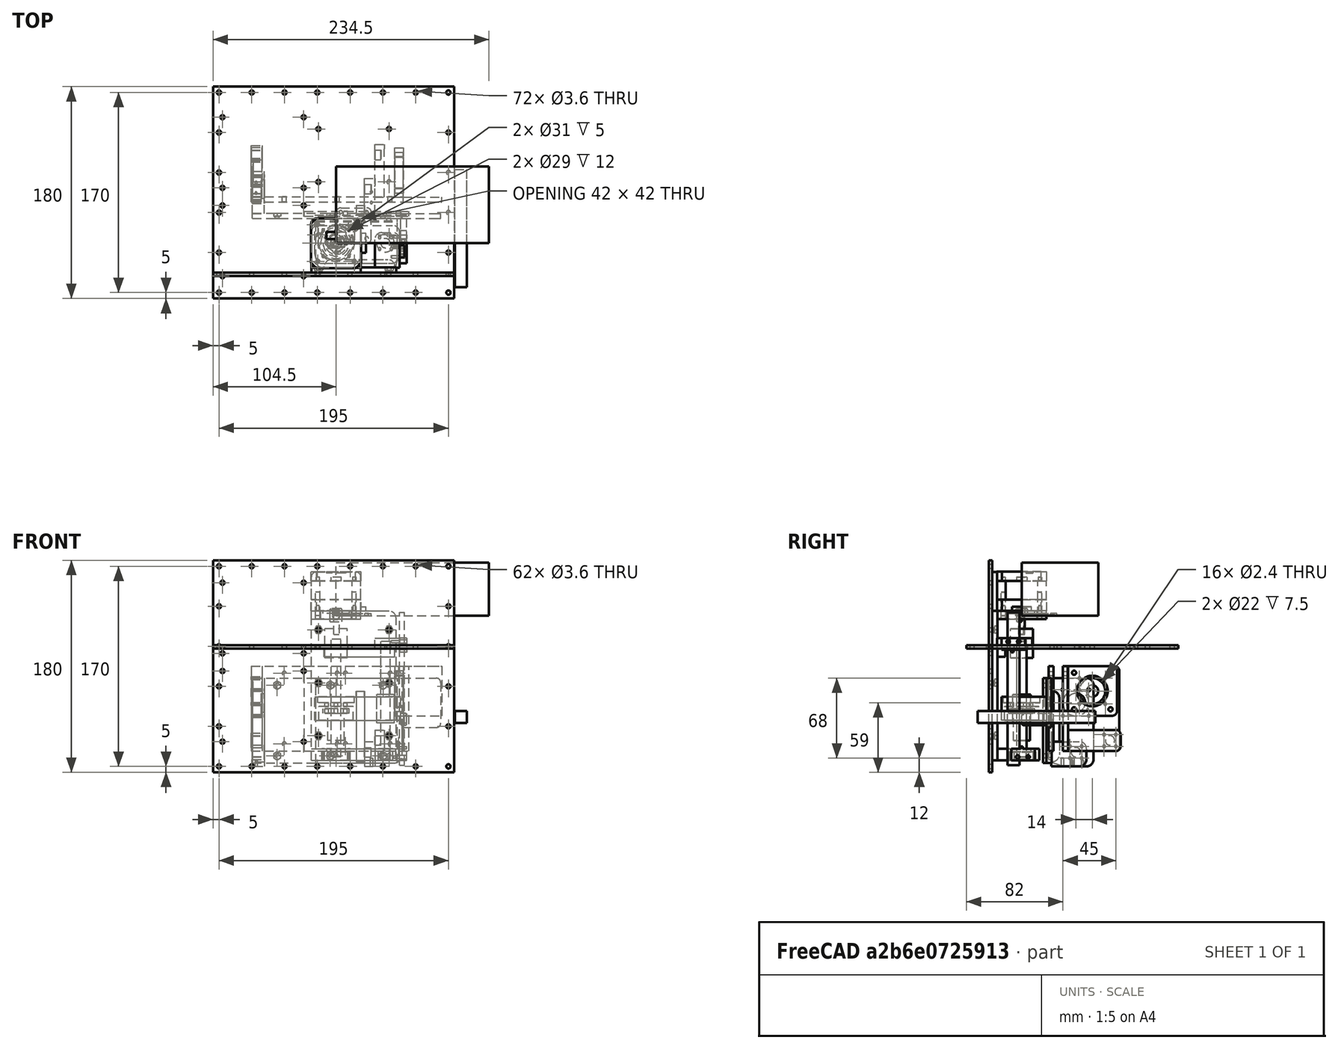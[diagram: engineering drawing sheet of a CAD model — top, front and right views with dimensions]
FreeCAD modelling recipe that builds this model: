
FCSTD DOCUMENT  (FreeCAD 0.18.4R)
Label: small_moving_desk
License: All rights reserved
LicenseURL: http://en.wikipedia.org/wiki/All_rights_reserved
objects: Part::Cylinder×33, Part::Box×21, Part::FeaturePython×18, Part::Cut×14, Part::MultiFuse×12, Part::Fillet×10, App::Part×9, PartDesign::FeatureBase×9, PartDesign::Body×9, Part::Feature×7, Part::Compound×5, Path::FeaturePython×4, Mesh::Feature×1, App::FeaturePython×1, App::DocumentObjectGroup×1, Path::FeatureCompoundPython×1, Part::RegularPolygon×1, Part::Extrusion×1
note: 141 computed .brp shape members not serialized (recipe doc carries the construction recipe); baked Part::Feature solids carry a one-line shape summary decoded from their .brp

FEATURE [Part::Feature] Pocket003Body001  label="StepperBody"
  Placement = pos=(0,0,4) rot=(0,0,1;0rad)
  shape: bbox 46.6 x 42.3 x 53.35 mm, 70 faces (baked)
FEATURE [Part::Box] Box  label="motor side cube"
  AttacherType = Attacher::AttachEngine3D
  Height = 7
  Length = 42
  Placement = pos=(-21,-21,-3) rot=(0,0,1;0rad)
  Width = 42
FEATURE [Part::Cylinder] Cylinder  label="motor central hole"
  Angle = 360
  AttacherType = Attacher::AttachEngine3D
  Height = 20
  Radius = 13
FEATURE [Part::Cylinder] Cylinder001  label="motor attachment hole"
  Angle = 360
  AttacherType = Attacher::AttachEngine3D
  Height = 20
  Placement = pos=(-15.5,-15.5,0) rot=(0,0,1;0rad)
  Radius = 1.8
FEATURE [Part::FeaturePython] Array  label="motor attachment hole array"  # Draft array (typed FeaturePython)
  Angle = 360
  ArrayType = 0
  Axis = (0,0,1)
  Base = -> Cylinder001
  Center = (0,0,0)
  Fuse = false
  IntervalAxis = (0,0,0)
  IntervalX = (31,0,0)
  IntervalY = (0,31,0)
  IntervalZ = (0,0,1)
  NumberPolar = 1
  NumberX = 2
  NumberY = 2
  NumberZ = 1
FEATURE [Part::Cylinder] Cylinder002
  Angle = 360
  AttacherType = Attacher::AttachEngine3D
  Height = 25
  Placement = pos=(0,0,-36) rot=(0,0,1;0rad)
  Radius = 9.5
FEATURE [Part::Cylinder] Cylinder003  label="lead cylinder"
  Angle = 360
  AttacherType = Attacher::AttachEngine3D
  Height = 100
  Placement = pos=(0,0,-120) rot=(0,0,1;0rad)
  Radius = 4
FEATURE [Part::Cylinder] Cylinder004  label="backlash nut cylinder"
  Angle = 360
  AttacherType = Attacher::AttachEngine3D
  Height = 23
  Placement = pos=(0,0,-23) rot=(0,0,1;0rad)
  Radius = 7
FEATURE [Part::Cylinder] Cylinder005  label="backlash nut disk"
  Angle = 360
  AttacherType = Attacher::AttachEngine3D
  Height = 4
  Radius = 11
FEATURE [Part::Cylinder] Cylinder006  label="Cylinder004"
  Angle = 360
  AttacherType = Attacher::AttachEngine3D
  Height = 20
  Placement = pos=(0,-8,-5) rot=(0,0,1;0rad)
  Radius = 1.5
FEATURE [Part::FeaturePython] Array001  # Draft array (typed FeaturePython)
  Angle = 360
  ArrayType = 1
  Axis = (0,0,1)
  Base = -> Cylinder006
  Center = (0,0,0)
  Fuse = false
  IntervalAxis = (0,0,0)
  IntervalX = (1,0,0)
  IntervalY = (0,1,0)
  IntervalZ = (0,0,1)
  NumberPolar = 4
  NumberX = 2
  NumberY = 2
  NumberZ = 1
FEATURE [Part::Cut] Cut
  Base = -> Cylinder005
  Tool = -> Array001
FEATURE [Part::MultiFuse] Fusion  label="backlash nut union"
  Placement = pos=(0,0,-83) rot=(0,0,1;0rad)
  Shapes = -> [Cut,Cylinder004]
FEATURE [Part::MultiFuse] Fusion001
  Placement = pos=(0,0,-5) rot=(0,0,1;0rad)
  Shapes = -> [Cylinder,Array]
FEATURE [Part::Cylinder] Cylinder007  label="rod cylinder"
  Angle = 360
  AttacherType = Attacher::AttachEngine3D
  Height = 100
  Placement = pos=(42,0,-122) rot=(0,0,1;0rad)
  Radius = 4
FEATURE [Part::Box] Box001  label="nut disk cube"
  AttacherType = Attacher::AttachEngine3D
  Height = 20
  Length = 69
  Placement = pos=(-17,-17,-89) rot=(0,0,1;0rad)
  Width = 36
FEATURE [Part::Box] Box002  label="other side cube"
  AttacherType = Attacher::AttachEngine3D
  Height = 10
  Length = 75
  Placement = pos=(-21,-21,-123) rot=(0,0,1;0rad)
  Width = 36
FEATURE [Part::Cylinder] Cylinder008  label="side bearing cylinder"
  Angle = 360
  AttacherType = Attacher::AttachEngine3D
  Height = 7.5
  Placement = pos=(0,0,-123) rot=(0,0,1;0rad)
  Radius = 11
FEATURE [Part::Cylinder] Cylinder009  label="bearing"
  Angle = 360
  AttacherType = Attacher::AttachEngine3D
  Height = 7
  Placement = pos=(0,0,-123) rot=(0,0,1;0rad)
  Radius = 11
FEATURE [Part::Cylinder] Cylinder010  label="rod hole cylinder"
  Angle = 360
  AttacherType = Attacher::AttachEngine3D
  Height = 102
  Placement = pos=(42,0,-124) rot=(0,0,1;0rad)
  Radius = 4
FEATURE [Part::Cut] Cut002  label="motor side cut"
  Base = -> Box
  Tool = -> Fusion001
FEATURE [Part::Box] Box003  label="bottom cube"
  AttacherType = Attacher::AttachEngine3D
  Height = 127
  Length = 72
  Placement = pos=(-21,-25,-123) rot=(0,0,1;0rad)
  Width = 4.5
FEATURE [Part::Box] Box004  label="rod holder cube"
  AttacherType = Attacher::AttachEngine3D
  Height = 9
  Length = 21
  Placement = pos=(33,-21,-28) rot=(0,0,1;0rad)
  Width = 30
FEATURE [Part::Cylinder] Cylinder011  label="side bearing central hole cylinder"
  Angle = 360
  AttacherType = Attacher::AttachEngine3D
  Height = 15
  Placement = pos=(0,0,-128) rot=(0,0,1;0rad)
  Radius = 8
FEATURE [Part::Feature] Array001001  label="backlash nut holes"
  Placement = pos=(0,0,-82) rot=(0,0,1;0rad)
  shape: bbox 19 x 19 x 20 mm, 12 faces, 4 solids (baked)
FEATURE [Part::Cylinder] Cylinder012  label="lead hole cylinder"
  Angle = 360
  AttacherType = Attacher::AttachEngine3D
  Height = 40
  Placement = pos=(0,0,-94) rot=(0,0,1;0rad)
  Radius = 4.4
FEATURE [Part::Cylinder] Cylinder013  label="rod bearing cylinder"
  Angle = 360
  AttacherType = Attacher::AttachEngine3D
  Height = 24
  Placement = pos=(42,0,-91) rot=(0,0,1;0rad)
  Radius = 7.5
FEATURE [Part::MultiFuse] Fusion005  label="rod fusion"
  Shapes = -> [Cylinder013,Cylinder007]
FEATURE [Part::Compound] Compound
  Links = -> [Pocket003Body001,Cylinder002,Cylinder003,Fusion,Cylinder009,Cylinder007,Fusion005,Cylinder013]
FEATURE [App::Part] Part001  label="stepper construction mockup"
  Group = -> [Pocket003Body001,Cylinder002,Cylinder003,Cylinder004,Cylinder005,Fusion,Cylinder006,Array001,Cut,Compound,Cylinder009,Cylinder007,Cylinder013]
  Origin = -> Origin001
FEATURE [Part::Cylinder] Cylinder014  label="rod cover hole"
  Angle = 360
  AttacherType = Attacher::AttachEngine3D
  Height = 20
  Placement = pos=(37,-5,-129) rot=(0,0,1;0rad)
  Radius = 1.2
FEATURE [Part::FeaturePython] Array001002  label="rod holder hole array"  # Draft array (typed FeaturePython)
  Angle = 360
  ArrayType = 0
  Axis = (0,0,1)
  Base = -> Cylinder014
  Center = (0,0,0)
  Fuse = false
  IntervalAxis = (0,0,0)
  IntervalX = (10,0,0)
  IntervalY = (0,10,0)
  IntervalZ = (0,0,1)
  NumberPolar = 1
  NumberX = 2
  NumberY = 2
  NumberZ = 1
FEATURE [Part::Fillet] Fillet001  label="motor side fillet"
  Base = -> Cut002
  Edges = 2 edges r=4: [Edge3,Edge16]
FEATURE [Part::Box] Box005  label="bottom cube motor side"
  AttacherType = Attacher::AttachEngine3D
  Height = 34
  Length = 42
  Placement = pos=(-21,-25,3) rot=(0,0,1;0rad)
  Width = 4
FEATURE [Part::Cylinder] Cylinder015  label="bottom hole cylinder"
  Angle = 360
  AttacherType = Attacher::AttachEngine3D
  Height = 20
  Placement = pos=(-15,-31,-12) rot=(-1,0,0;1.5708rad)
  Radius = 1.8
FEATURE [Part::Cylinder] Cylinder016  label="Cylinder006"
  Angle = 360
  AttacherType = Attacher::AttachEngine3D
  Height = 20
  Placement = pos=(-11,-11,-129) rot=(0,0,1;0rad)
  Radius = 1.2
FEATURE [Part::FeaturePython] Array001004  label="lead holder hole array"  # Draft array (typed FeaturePython)
  Angle = 360
  ArrayType = 0
  Axis = (0,0,1)
  Base = -> Cylinder016
  Center = (0,0,0)
  Fuse = false
  IntervalAxis = (0,0,0)
  IntervalX = (22,0,0)
  IntervalY = (0,22,0)
  IntervalZ = (0,0,1)
  NumberPolar = 1
  NumberX = 2
  NumberY = 2
  NumberZ = 1
FEATURE [Part::Cylinder] Cylinder017  label="rod bearing cylinder001"
  Angle = 360
  AttacherType = Attacher::AttachEngine3D
  Height = 24
  Placement = pos=(42,0,-90) rot=(0,0,1;0rad)
  Radius = 7.5
FEATURE [Part::Cylinder] Cylinder018  label="backlash nut disk hole"
  Angle = 360
  AttacherType = Attacher::AttachEngine3D
  Height = 20
  Placement = pos=(0,0,-97) rot=(0,0,1;0rad)
  Radius = 14.5
FEATURE [Part::Feature] Compound001001  label="bottom compound001"
  Placement = pos=(53,60,-64) rot=(0,1,0;1.5708rad)
  shape: bbox 162 x 49 x 72 mm, 58 faces, 4 solids (baked)
FEATURE [Part::Box] Box006  label="plate cube"
  AttacherType = Attacher::AttachEngine3D
  Height = 72
  Length = 69
  Placement = pos=(-17,18,-125) rot=(0,0,1;0rad)
  Width = 3
FEATURE [Part::Cylinder] Cylinder019  label="bottom hole cylinder001"
  Angle = 360
  AttacherType = Attacher::AttachEngine3D
  Height = 20
  Placement = pos=(59,14,53) rot=(-1,0,0;1.5708rad)
  Radius = 1.8
FEATURE [Part::Fillet] Fillet002  label="lead rod connector fillet"
  Base = -> Box001
  Edges = 2 edges r=4: [Edge1,Edge5]
FEATURE [Part::Box] Box007  label="bearing cover cube"
  AttacherType = Attacher::AttachEngine3D
  Height = 2
  Length = 30
  Width = 30
FEATURE [Part::Cylinder] Cylinder020  label="Cylinder007"
  Angle = 360
  AttacherType = Attacher::AttachEngine3D
  Height = 20
  Placement = pos=(4,4,-7) rot=(0,0,1;0rad)
  Radius = 1.6
FEATURE [Part::FeaturePython] Array001006  label="lead holder hole array001"  # Draft array (typed FeaturePython)
  Angle = 360
  ArrayType = 0
  Axis = (0,0,1)
  Base = -> Cylinder020
  Center = (0,0,0)
  Fuse = false
  IntervalAxis = (0,0,0)
  IntervalX = (22,0,0)
  IntervalY = (0,22,0)
  IntervalZ = (0,0,1)
  NumberPolar = 1
  NumberX = 2
  NumberY = 2
  NumberZ = 1
FEATURE [Part::Cylinder] Cylinder021  label="side bearing central hole cylinder001"
  Angle = 360
  AttacherType = Attacher::AttachEngine3D
  Height = 15
  Placement = pos=(15,15,-4) rot=(0,0,1;0rad)
  Radius = 5
FEATURE [Part::MultiFuse] Fusion008
  Shapes = -> [Array001006,Cylinder021]
FEATURE [Part::Cut] Cut005  label="bearing cover cut"
  Base = -> Box007
  Tool = -> Fusion008
FEATURE [Part::Box] Box008  label="bearing cover cube001"
  AttacherType = Attacher::AttachEngine3D
  Height = 1
  Length = 16
  Width = 16
FEATURE [Part::Cylinder] Cylinder022  label="Cylinder008"
  Angle = 360
  AttacherType = Attacher::AttachEngine3D
  Height = 20
  Placement = pos=(3,3,-6) rot=(0,0,1;0rad)
  Radius = 1.6
FEATURE [Part::FeaturePython] Array001007  label="rod holder hole array001"  # Draft array (typed FeaturePython)
  Angle = 360
  ArrayType = 0
  Axis = (0,0,1)
  Base = -> Cylinder022
  Center = (0,0,0)
  Fuse = false
  IntervalAxis = (0,0,0)
  IntervalX = (10,0,0)
  IntervalY = (0,10,0)
  IntervalZ = (0,0,1)
  NumberPolar = 1
  NumberX = 2
  NumberY = 2
  NumberZ = 1
FEATURE [Part::Cut] Cut006  label="rod cover cut"
  Base = -> Box008
  Tool = -> Array001007
FEATURE [Part::Fillet] Fillet003  label="rod cover fillet"
  Base = -> Cut006
  Edges = 4 edges r=4: [Edge1,Edge3,Edge6,Edge15]
FEATURE [App::Part] Part003  label="rod cover part"
  Group = -> [Box008,Cylinder022,Array001007,Cut006,Fillet003]
  Origin = -> Origin003
  Placement = pos=(34,-8,-126) rot=(0,0,1;0rad)
FEATURE [Part::Cylinder] Cylinder024  label="backlash nut disk hole001"
  Angle = 360
  AttacherType = Attacher::AttachEngine3D
  Height = 10
  Placement = pos=(0,0,-74) rot=(0,0,1;0rad)
  Radius = 15.5
FEATURE [Part::Fillet] Fillet004  label="bearing cover fillet"
  Base = -> Cut005
  Edges = 4 edges r=4: [Edge1,Edge3,Edge6,Edge16]
FEATURE [App::Part] Part002  label="bearing cover part"
  Group = -> [Box007,Cylinder020,Array001006,Cut005,Cylinder021,Fusion008,Fillet004]
  Origin = -> Origin002
  Placement = pos=(-15,-15,-126) rot=(0,0,1;0rad)
FEATURE [Part::Fillet] Fillet005
  Base = -> Box005
  Edges = 2 edges r=4: [Edge2,Edge6]
FEATURE [Part::Fillet] Fillet006
  Base = -> Box003
  Edges = 1 edges r=6: [Edge6]
FEATURE [Part::MultiFuse] Fusion006  label="bottom fusion"
  Shapes = -> [Fillet005,Fillet006]
FEATURE [Part::Box] Box009  label="nut disk cube001"
  AttacherType = Attacher::AttachEngine3D
  Height = 20
  Length = 73
  Placement = pos=(-18,-17,-89) rot=(0,0,1;0rad)
  Width = 41
FEATURE [Part::Fillet] Fillet007  label="lead rod connector fillet001"
  Base = -> Box009
  Edges = 2 edges r=8: [Edge1,Edge5]
FEATURE [Part::Box] Box011  label="plate cube002"
  AttacherType = Attacher::AttachEngine3D
  Height = 72
  Length = 89
  Placement = pos=(-27,23,-125) rot=(0,0,1;0rad)
  Width = 4
FEATURE [Part::FeaturePython] Array001010  label="bottom hole array004"  # Draft array (typed FeaturePython)
  Angle = 360
  ArrayType = 0
  Axis = (0,0,1)
  Base = -> Cylinder019
  Center = (0,0,0)
  Fuse = false
  IntervalAxis = (0,0,0)
  IntervalX = (60,0,0)
  IntervalY = (0,1,0)
  IntervalZ = (0,0,-45)
  NumberPolar = 1
  NumberX = 2
  NumberY = 1
  NumberZ = 3
  Placement = pos=(0,0,0) rot=(0,1,0;1.5708rad)
FEATURE [Part::Cut] Cut010  label="top plate cut002"
  Base = -> Box011
  Placement = pos=(0,0,10) rot=(0,0,1;0rad)
  Tool = -> Array001010
FEATURE [Part::Cylinder] Cylinder026  label="bottom hole cylinder003"
  Angle = 360
  AttacherType = Attacher::AttachEngine3D
  Height = 20
  Placement = pos=(59,14,45) rot=(-1,0,0;1.5708rad)
  Radius = 1.8
FEATURE [Part::FeaturePython] Array001005  label="bottom hole array001"  # Draft array (typed FeaturePython)
  Angle = 360
  ArrayType = 0
  Axis = (0,0,1)
  Base = -> Cylinder026
  Center = (0,0,0)
  Fuse = false
  IntervalAxis = (0,0,0)
  IntervalX = (60,0,0)
  IntervalY = (0,1,0)
  IntervalZ = (0,0,-45)
  NumberPolar = 1
  NumberX = 2
  NumberY = 1
  NumberZ = 3
  Placement = pos=(0,0,0) rot=(0,1,0;1.5708rad)
FEATURE [Part::MultiFuse] Fusion004  label="nut disk hole union"
  Shapes = -> [Cylinder010,Array001001,Cylinder012,Cylinder017,Cylinder018,Array001005,Cylinder024]
FEATURE [Part::Cut] Cut003  label="top moving cut"
  Base = -> Fillet002
  Tool = -> Fusion004
FEATURE [Part::Cut] Cut007  label="top plate cut"
  Base = -> Box006
  Tool = -> Array001005
FEATURE [Part::Compound] Compound001002  label="moving compound"
  Links = -> [Cut003,Cut007]
FEATURE [Part::Cut] Cut008  label="top moving cut001"
  Base = -> Fillet007
  Tool = -> Fusion004
FEATURE [PartDesign::FeatureBase] Clone002
  BaseFeature = -> Compound001002
FEATURE [PartDesign::Body] Body002  label="bottom moving body"
  BaseFeature = -> Compound001002
  Group = -> [Clone002]
  Origin = -> Origin007
  Tip = -> Clone002
FEATURE [Part::Box] Box012  label="volume of controller cube"
  AttacherType = Attacher::AttachEngine3D
  Height = 45
  Length = 130
  Width = 65
FEATURE [App::Part] Part005  label="stepper controller mockup"
  Group = -> [Box012]
  Origin = -> Origin008
FEATURE [Part::Box] Box013  label="base plate cube"
  AttacherType = Attacher::AttachEngine3D
  Height = 180
  Length = 205
  Placement = pos=(-104.5,-28,-133) rot=(0,0,1;0rad)
  Width = 3
FEATURE [Part::Box] Box014  label="test cube"
  AttacherType = Attacher::AttachEngine3D
  Height = 10
  Length = 10
  Placement = pos=(101,-37.5,-91) rot=(0,0,1;0rad)
  Width = 100
FEATURE [Mesh::Feature] _560Bracket  label="2560Bracket"
  Placement = pos=(27.825,-18.68,518.342) rot=(-0.57735,0.57735,0.57735;2.0944rad)
FEATURE [Part::Feature] _560Bracket001  label="_560Bracket"
  Placement = pos=(0,-6,32) rot=(0,0,1;0rad)
  shape: bbox 78 x 10 x 107 mm, 2252 faces, 0 solids (baked)
FEATURE [Part::Cylinder] Cylinder027  label="mega hole"
  Angle = 360
  AttacherType = Attacher::AttachEngine3D
  Height = 20
  Placement = pos=(-96.5,-34,-47) rot=(-1,0,0;1.5708rad)
  Radius = 1.8
FEATURE [Part::FeaturePython] Array001011  label="mega hole array"  # Draft array (typed FeaturePython)
  Angle = 360
  ArrayType = 0
  Axis = (0,0,1)
  Base = -> Cylinder027
  Center = (0,0,0)
  Fuse = false
  IntervalAxis = (0,0,0)
  IntervalX = (69,0,0)
  IntervalY = (0,1,0)
  IntervalZ = (0,0,75)
  NumberPolar = 1
  NumberX = 2
  NumberY = 1
  NumberZ = 2
FEATURE [Part::Cylinder] Cylinder028  label="attachment hole"
  Angle = 360
  AttacherType = Attacher::AttachEngine3D
  Height = 20
  Placement = pos=(-99.5,-37,-128) rot=(-1,0,0;1.5708rad)
  Radius = 1.8
FEATURE [Part::FeaturePython] Array001012  label="attachment hole z array"  # Draft array (typed FeaturePython)
  Angle = 360
  ArrayType = 0
  Axis = (0,0,1)
  Base = -> Cylinder028
  Center = (0,0,0)
  Fuse = false
  IntervalAxis = (0,0,0)
  IntervalX = (1,0,0)
  IntervalY = (0,1,0)
  IntervalZ = (0,0,34)
  NumberPolar = 1
  NumberX = 1
  NumberY = 1
  NumberZ = 6
FEATURE [Part::Cylinder] Cylinder029  label="attachment hole001"
  Angle = 360
  AttacherType = Attacher::AttachEngine3D
  Height = 20
  Placement = pos=(-99.5,-37,-128) rot=(-1,0,0;1.5708rad)
  Radius = 1.8
FEATURE [Part::FeaturePython] Array001013  label="attachment hole x array"  # Draft array (typed FeaturePython)
  Angle = 360
  ArrayType = 0
  Axis = (0,0,1)
  Base = -> Cylinder029
  Center = (0,0,0)
  Fuse = false
  IntervalAxis = (0,0,0)
  IntervalX = (27.86,0,0)
  IntervalY = (0,1,0)
  IntervalZ = (0,0,1)
  NumberPolar = 1
  NumberX = 8
  NumberY = 1
  NumberZ = 1
FEATURE [Part::FeaturePython] Array001014  label="attachment hole x by z array"  # Draft array (typed FeaturePython)
  Angle = 360
  ArrayType = 0
  Axis = (0,0,1)
  Base = -> Array001013
  Center = (0,0,0)
  Fuse = false
  IntervalAxis = (0,0,0)
  IntervalX = (1,0,0)
  IntervalY = (0,1,0)
  IntervalZ = (0,0,170)
  NumberPolar = 1
  NumberX = 1
  NumberY = 1
  NumberZ = 2
FEATURE [Part::FeaturePython] Array001015  label="attachment hole z by x array"  # Draft array (typed FeaturePython)
  Angle = 360
  ArrayType = 0
  Axis = (0,0,1)
  Base = -> Array001012
  Center = (0,0,0)
  Fuse = false
  IntervalAxis = (0,0,0)
  IntervalX = (195,0,0)
  IntervalY = (0,1,0)
  IntervalZ = (0,0,1)
  NumberPolar = 1
  NumberX = 2
  NumberY = 1
  NumberZ = 1
FEATURE [Part::Feature] Compound001004_solid001  label="bottom all plate compound (Solid)"
  shape: bbox 205 x 180 x 3 mm, 42 faces (baked)
FEATURE [App::FeaturePython] SetupSheet  # Path/CAM operation (typed FeaturePython)
  ClearanceHeightExpression = OpStockZMax+SetupSheet.ClearanceHeightOffset
  ClearanceHeightOffset = 0
  FinalDepthExpression = OpFinalDepth
  HorizRapid = 100
  SafeHeightExpression = OpStockZMax+SetupSheet.SafeHeightOffset
  SafeHeightOffset = 0
  StartDepthExpression = OpStartDepth
  StepDownExpression = OpToolDiameter
  VertRapid = 100
FEATURE [Path::FeaturePython] T3__laser  label="T3: laser"  # Path/CAM operation (typed FeaturePython)
  HorizFeed = 0.5
  HorizRapid = 100
  SpindleDir = 0
  SpindleSpeed = 1000
  ToolNumber = 3
  VertFeed = 0.5
  VertRapid = 100
  expr: VertRapid = SetupSheet.VertRapid
  expr: HorizRapid = SetupSheet.HorizRapid
FEATURE [Path::FeaturePython] Contour  # Path/CAM operation (typed FeaturePython)
  Active = true
  AreaParams:
    Tolerance = 1e-07
    FitArcs = True
    Simplify = False
    CleanDistance = 0.0
    Accuracy = 0.01
    Unit = 1.0
    MinArcPoints = 4
    MaxArcPoints = 100
    ClipperScale = 10000000.0
    Fill = 0
    Coplanar = 2
    Reorient = True
    Outline = False
    Explode = False
    OpenMode = 0
    Deflection = 0.01
    SubjectFill = 0
    ClipFill = 0
    Offset = 0.1
    ExtraPass = 0
    Stepover = 0.0
    LastStepover = 0.0
    JoinType = 0
    EndType = 0
    MiterLimit = 2.0
    RoundPrecision = 0.0
    PocketMode = 0
    ToolRadius = 1.0
    PocketExtraOffset = 0.0
    PocketStepover = 0.0
    PocketLastStepover = 0.0
    FromCenter = False
    Angle = 45.0
    AngleShift = 0.0
    Shift = 0.0
    Thicken = False
    SectionCount = -1
    Stepdown = 1.0
    SectionOffset = 0.0
    SectionTolerance = 1e-06
    SectionMode = 2
    Project = False
  ClearanceHeight = 1
  Direction = 0
  FinalDepth = 0
  JoinType = 0
  MiterLimit = 0.1
  OffsetExtra = 0
  OpFinalDepth = -28
  OpStartDepth = -25
  OpStockZMax = -25
  OpStockZMin = -28
  OpToolDiameter = 0.2
  PathParams = {'orientation': 1, 'feedrate': 0.5, 'feedrate_v': 0.5, 'verbose': True, 'resume_height': 1.0, 'retraction': 1.0, 'return_end': True, 'preamble': False}
  SafeHeight = 1
  Side = 0
  StartDepth = 0.1
  StartPoint = (0,0,0)
  StepDown = 0.2
  ToolController = -> T3__laser
  UseComp = true
  UseStartPoint = false
  expr: StepDown = OpToolDiameter
FEATURE [Part::Feature] _560Bracket002  label="_560Bracket001"
  Placement = pos=(0,-6,-28) rot=(0,0,1;0rad)
  shape: bbox 78 x 10 x 107 mm, 2252 faces, 0 solids (baked)
FEATURE [PartDesign::FeatureBase] Clone007
  BaseFeature = -> Array001011
FEATURE [PartDesign::Body] Body004  label="mega hole array clone"
  BaseFeature = -> Array001011
  Group = -> [Clone007]
  Origin = -> Origin010
  Placement = pos=(0,0,-60) rot=(0,0,1;0rad)
  Tip = -> Clone007
FEATURE [Part::Feature] Compound001004001_solid  label="bottom all plate compound001 (Solid)"
  shape: bbox 205 x 180 x 3 mm, 46 faces (baked)
FEATURE [Part::FeaturePython] Clone008  label="Stock-Array"  # Draft clone (typed FeaturePython)
  AttacherType = Attacher::AttachEngine3D
  Fuse = false
  Objects = -> [Array]
  PathResource = Stock
  Scale = (1,1,1)
  StockType = Unknown
FEATURE [Part::FeaturePython] Clone009  label="Model-bottom all plate compound001 (Solid)"  # Draft clone (typed FeaturePython)
  AttacherType = Attacher::AttachEngine3D
  Fuse = false
  Objects = -> [Compound001004001_solid]
  PathResource = Model
  Scale = (1,1,1)
FEATURE [App::DocumentObjectGroup] Model
  Group = -> [Clone009]
FEATURE [Path::FeaturePython] Engrave  # Path/CAM operation (typed FeaturePython)
  Active = true
  Base = -> [Clone009]
  ClearanceHeight = 1
  FinalDepth = 0
  OpFinalDepth = -25.2
  OpStartDepth = -25
  OpStockZMax = 20
  OpStockZMin = 0
  OpToolDiameter = 0.2
  SafeHeight = 1
  StartDepth = 0
  StartVertex = 0
  StepDown = 0.2
  ToolController = -> T3__laser
  expr: StepDown = OpToolDiameter
FEATURE [Path::FeatureCompoundPython] Operations  # Path/CAM operation (typed FeaturePython)
  Group = -> [Contour,Engrave]
  UsePlacements = false
FEATURE [Path::FeaturePython] Job  label="all bottom job"  # Path/CAM operation (typed FeaturePython)
  GeometryTolerance = 0.01
  Model = -> Model
  Operations = -> Operations
  PostProcessor = 1
  PostProcessorOutputFile = <userpath>/work/roborep/freecad/small_moving_desk/all_bottom.gcode
  SetupSheet = -> SetupSheet
  Stock = -> Clone008
  ToolController = -> [T3__laser]
FEATURE [Part::Cylinder] Cylinder030  label="internal cylinder"
  Angle = 360
  AttacherType = Attacher::AttachEngine3D
  Height = 10
  Placement = pos=(0,0,1) rot=(0,0,1;0rad)
  Radius = 3
FEATURE [Part::Cylinder] Cylinder031  label="external cylinder"
  Angle = 360
  AttacherType = Attacher::AttachEngine3D
  Height = 6
  Radius = 5
FEATURE [Part::Cylinder] Cylinder032  label="hole cylinder"
  Angle = 360
  AttacherType = Attacher::AttachEngine3D
  Height = 10
  Radius = 2
FEATURE [Part::MultiFuse] Fusion010
  Shapes = -> [Cylinder030,Cylinder032]
FEATURE [Part::Cut] Cut012
  Base = -> Cylinder031
  Tool = -> Fusion010
FEATURE [Part::Fillet] Fillet008
  Base = -> Cut012
  Edges = 1 edges r=1: [Edge1]
FEATURE [App::Part] Part006  label="leg part"
  Group = -> [Cylinder032,Cylinder030,Fusion010,Cylinder031,Cut012,Fillet008]
  Origin = -> Origin011
FEATURE [Part::Box] Box015  label="end stop pusher"
  AttacherType = Attacher::AttachEngine3D
  Height = 10
  Length = 5
  Placement = pos=(55,0,-93) rot=(0,0,1;0rad)
  Width = 24
FEATURE [Part::Fillet] Fillet009  label="end stop pusher fillet"
  Base = -> Box015
  Edges = 6 edges: [Edge4 r=1,Edge5 r=2,Edge6 r=1,Edge8 r=1,Edge9 r=2,Edge10 r=2]
FEATURE [Part::Compound] Compound001003  label="toller moving compound"
  Links = -> [Cut008,Cut010,Fillet009]
FEATURE [Part::Box] Box016  label="end stop body cube"
  AttacherType = Attacher::AttachEngine3D
  Height = 10
  Length = 6
  Width = 20
FEATURE [Part::Box] Box017  label="end stop pushee cube"
  AttacherType = Attacher::AttachEngine3D
  Height = 2
  Length = 6
  Placement = pos=(0,8,10) rot=(0,0,1;0rad)
  Width = 2
FEATURE [Part::MultiFuse] Fusion011  label="end stop body fusion"
  Shapes = -> [Box017,Box016]
FEATURE [Part::Cylinder] Cylinder033  label="end body hole"
  Angle = 360
  AttacherType = Attacher::AttachEngine3D
  Height = 10
  Placement = pos=(-2,5.5,3) rot=(0,1,0;1.5708rad)
  Radius = 1.5
FEATURE [Part::FeaturePython] Array001016  label="end stop hole array"  # Draft array (typed FeaturePython)
  Angle = 360
  ArrayType = 0
  Axis = (0,0,1)
  Base = -> Cylinder033
  Center = (0,0,0)
  Fuse = false
  IntervalAxis = (0,0,0)
  IntervalX = (1,0,0)
  IntervalY = (0,9,0)
  IntervalZ = (0,0,1)
  NumberPolar = 1
  NumberX = 1
  NumberY = 2
  NumberZ = 1
FEATURE [Part::Cut] Cut013  label="end stop cut"
  Base = -> Fusion011
  Tool = -> Array001016
FEATURE [PartDesign::FeatureBase] Clone010
  BaseFeature = -> Cut013
FEATURE [PartDesign::Body] Body005  label="end stop clone"
  BaseFeature = -> Cut013
  Group = -> [Clone010]
  Origin = -> Origin013
  Placement = pos=(54,-9,-123) rot=(0,0,1;0rad)
  Tip = -> Clone010
FEATURE [Part::Box] Box018  label="bottom removal cube"
  AttacherType = Attacher::AttachEngine3D
  Height = 10
  Length = 10
  Placement = pos=(50.29,-22.17,-123) rot=(0,0,-1;0.261799rad)
  Width = 14
FEATURE [App::Part] Part007  label="end stop mockup"
  Group = -> [Box016,Box017,Fusion011,Cylinder033,Array001016,Cut013]
  Origin = -> Origin012
FEATURE [Part::Cylinder] Cylinder034  label="end body narrow hole"
  Angle = 360
  AttacherType = Attacher::AttachEngine3D
  Height = 30
  Placement = pos=(49,-3.5,-120) rot=(0,1,0;1.5708rad)
  Radius = 1
FEATURE [Part::FeaturePython] Array001017  label="end stop narrow hole array"  # Draft array (typed FeaturePython)
  Angle = 360
  ArrayType = 0
  Axis = (0,0,1)
  Base = -> Cylinder034
  Center = (0,0,0)
  Fuse = false
  IntervalAxis = (0,0,0)
  IntervalX = (1,0,0)
  IntervalY = (0,9,0)
  IntervalZ = (0,0,1)
  NumberPolar = 1
  NumberX = 1
  NumberY = 2
  NumberZ = 1
FEATURE [Part::Box] Box019  label="limit cube"
  AttacherType = Attacher::AttachEngine3D
  Height = 7
  Length = 60
  Placement = pos=(-10,-21,-35) rot=(0,0,1;0rad)
  Width = 7
FEATURE [Part::MultiFuse] Fusion003
  Shapes = -> [Box002,Box004,Box019]
FEATURE [Part::Box] Box020  label="measuring cube"
  AttacherType = Attacher::AttachEngine3D
  Height = 130
  Length = 4
  Placement = pos=(54,-12,-127) rot=(0,0,1;0rad)
  Width = 10
FEATURE [PartDesign::FeatureBase] Clone011
  BaseFeature = -> Cut013
FEATURE [PartDesign::Body] Body006  label="end stop clone001"
  BaseFeature = -> Cut013
  Group = -> [Clone011]
  Origin = -> Origin014
  Placement = pos=(60,-17,-19) rot=(0,1,0;3.14159rad)
  Tip = -> Clone011
FEATURE [PartDesign::FeatureBase] Clone012
  BaseFeature = -> Array001017
FEATURE [PartDesign::Body] Body007  label="end stop narrow hole array001"
  BaseFeature = -> Array001017
  Group = -> [Clone012]
  Origin = -> Origin015
  Placement = pos=(-2,-8,98) rot=(0,0,1;0rad)
  Tip = -> Clone012
FEATURE [Part::MultiFuse] Fusion002
  Shapes = -> [Cylinder008,Cylinder010,Cylinder011,Array001002,Array001004,Box018,Array001017,Body007]
FEATURE [Part::Cut] Cut001  label="other side cut"
  Base = -> Fusion003
  Tool = -> Fusion002
FEATURE [Part::Fillet] Fillet  label="other side fillet"
  Base = -> Cut001
  Edges = 6 edges r=6: [Edge3,Edge13,Edge27,Edge28,Edge39,Edge59]
FEATURE [Part::RegularPolygon] RegularPolygon  label="nut hole polygon"
  AttacherType = Attacher::AttachEngine3D
  Circumradius = 3.5
  Polygon = 6
FEATURE [Part::Extrusion] Extrude  label="nut hole"
  Base = -> RegularPolygon
  Dir = (0,0,1)
  DirMode = 2
  FaceMakerClass = Part::FaceMakerBullseye
  LengthFwd = 5
  LengthRev = 0
  Placement = pos=(0,0,0) rot=(1,0,0;1.5708rad)
  Solid = true
  Symmetric = false
FEATURE [PartDesign::FeatureBase] Clone013
  BaseFeature = -> Extrude
  Placement = pos=(0,0,0) rot=(1,0,0;1.5708rad)
FEATURE [PartDesign::Body] Body008  label="nut hole clone"
  BaseFeature = -> Extrude
  Group = -> [Clone013]
  Origin = -> Origin017
  Placement = pos=(-15,-19,-12) rot=(0,0,1;0rad)
  Tip = -> Clone013
FEATURE [Part::MultiFuse] Fusion012  label="nut bottom hole"
  Placement = pos=(0,1,0) rot=(0,0,1;0rad)
  Shapes = -> [Cylinder015,Body008]
FEATURE [Part::FeaturePython] Array001003  label="bottom hole array"  # Draft array (typed FeaturePython)
  Angle = 360
  ArrayType = 0
  Axis = (0,0,1)
  Base = -> Fusion012
  Center = (0,0,0)
  Fuse = false
  IntervalAxis = (0,0,0)
  IntervalX = (60,0,0)
  IntervalY = (0,1,0)
  IntervalZ = (0,0,-45)
  NumberPolar = 1
  NumberX = 2
  NumberY = 1
  NumberZ = 3
FEATURE [Part::Cut] Cut004  label="bottom cut"
  Base = -> Fusion006
  Tool = -> Array001003
FEATURE [Part::Compound] Compound001  label="bottom compound"
  Links = -> [Fillet,Cut004]
FEATURE [App::Part] Part  label="desks part"
  Group = -> [Box,Cylinder,Cylinder001,Array,Fusion001,Box001,Box002,Cylinder008,Cut001,Cylinder010,Fusion002,Cut002,Box003,Box004,Fusion003,Cylinder011,Array001001,Cylinder012,Fusion004,Cut003,Cylinder014,Array001002,Fillet,Fillet001,Compound001,Box005,Cylinder015,Array001003,Fusion006,Cut004,Cylinder016,Array001004,Cylinder017,Cylinder018,Box006,Cylinder019,Array001005,Cylinder024,Fillet002,Fillet005,+22 more]
  Origin = -> Origin
FEATURE [PartDesign::FeatureBase] Clone
  BaseFeature = -> Compound001
FEATURE [PartDesign::Body] Body  label="bottom body"
  BaseFeature = -> Compound001
  Group = -> [Clone]
  Origin = -> Origin004
  Tip = -> Clone
FEATURE [PartDesign::FeatureBase] Clone001
  BaseFeature = -> Compound001
FEATURE [PartDesign::Body] Body001  label="top body"
  BaseFeature = -> Compound001
  Group = -> [Clone001]
  Origin = -> Origin006
  Placement = pos=(52,46,-74) rot=(0,1,0;1.5708rad)
  Tip = -> Clone001
FEATURE [PartDesign::FeatureBase] Clone003
  BaseFeature = -> Array001003
FEATURE [PartDesign::Body] Body003  label="bottom holes clone"
  BaseFeature = -> Array001003
  Group = -> [Clone003]
  Origin = -> Origin009
  Tip = -> Clone003
FEATURE [Part::MultiFuse] Fusion009  label="hole fusion"
  Shapes = -> [Array001011,Body003,Array001014,Array001015,Body004]
FEATURE [Part::Cut] Cut011  label="bottom all plate cut"
  Base = -> Box013
  Tool = -> Fusion009
FEATURE [Part::Compound] Compound001004  label="bottom all plate compound"
  Links = -> [Cut011]
FEATURE [App::Part] Part004  label="bottom all plate part"
  Group = -> [Body,Body001,Body002,Box013,Box014,_560Bracket,_560Bracket001,Cylinder027,Array001011,Body003,Fusion009,Cylinder028,Array001012,Cylinder029,Array001013,Array001014,Array001015,Cut011,Compound001004,_560Bracket002,Body004]
  Origin = -> Origin005
FEATURE [Part::Box] Box021  label="Cube"
  AttacherType = Attacher::AttachEngine3D
  Height = 10
  Length = 10
  Placement = pos=(-5,-4,-5) rot=(0,0,1;0rad)
  Width = 4
FEATURE [Part::Cut] Cut014  label="test cut"
  Base = -> Box021
  Tool = -> Extrude
FEATURE [App::Part] Part008  label="nut hole part"
  Group = -> [RegularPolygon,Extrude,Box021,Cut014]
  Origin = -> Origin016
